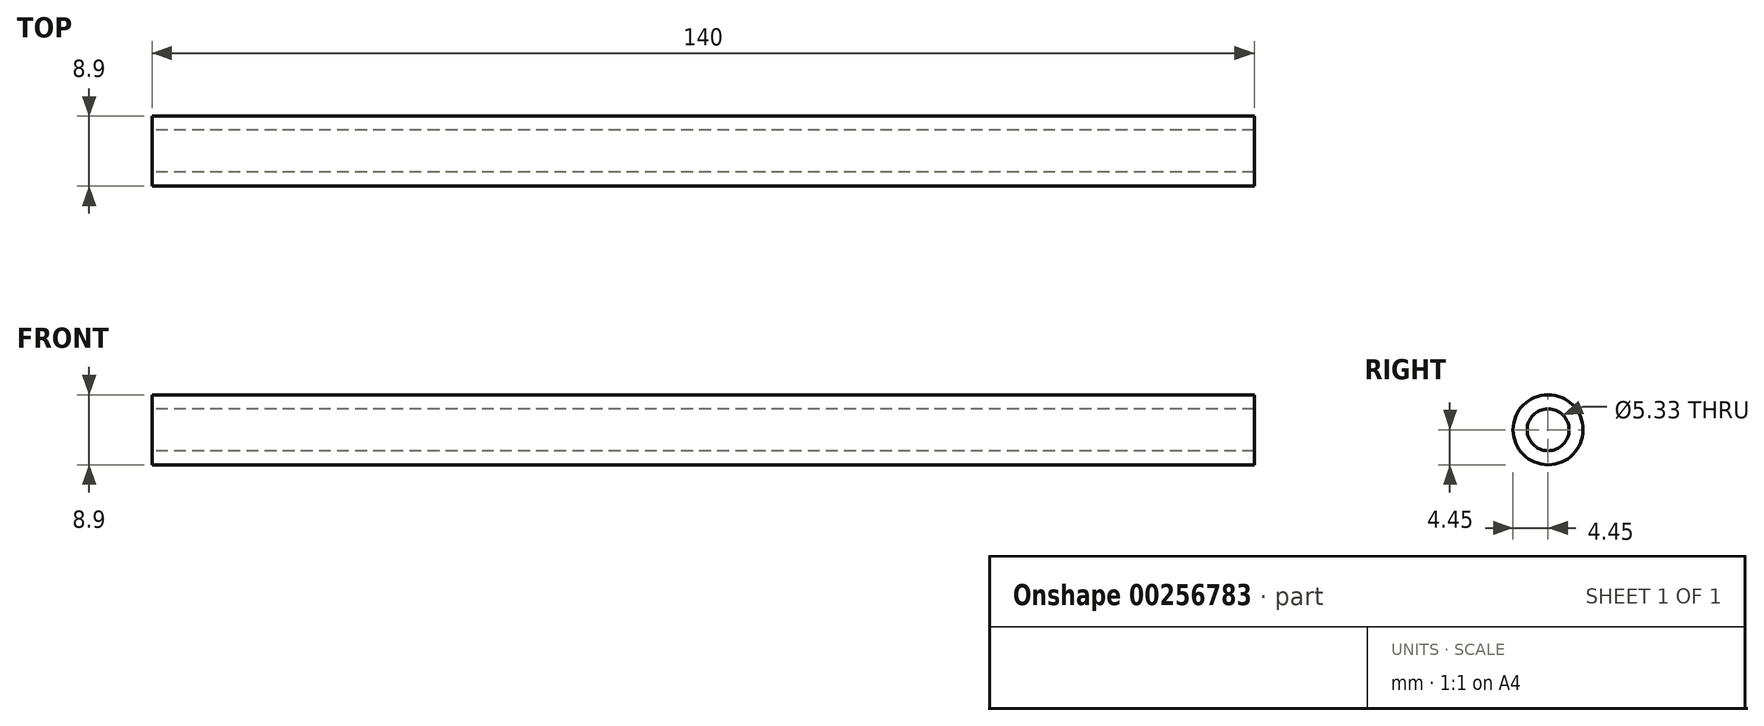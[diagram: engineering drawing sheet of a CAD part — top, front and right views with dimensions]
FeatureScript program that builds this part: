
annotation { "Feature Type Name" : "Feature", "Feature Type Description" : "" }
export const myFeature = defineFeature(function(context is Context, id is Id, definition is map)
    precondition{}
    {
        {
            var Q0;
            Q0=qCreatedBy(makeId("Right.planeOp"),FACE);
            var sketch = newSketch(context, id + "F0", { "sketchPlane" : qUnion([Q0])});
            skCircle(sketch, "E0", {"center": v(0, 0) * mm, "radius": 2.66 * mm});
            skCircle(sketch, "E1", {"center": v(0, 0) * mm, "radius": 4.45 * mm});
            skSolve(sketch);
        }
        {
            var Q0;
            Q0 = qSketchRegion(id + "F0", true);
            var Q1;
            Q1=makeQuery(id+"F0.imprint","IMPRINT",FACE,{"disambiguationData":[TD([[makeQuery(id+"F0.imprint","IMPRINT",EDGE,{"derivedFrom":sQuery(id+"F0.wireOp",EDGE,"E0")}),-1.0]])]});
            extrude(context, id + "F1", {"entities" : qUnion([Q0, Q1]), "depth" : 140 * mm});
        }
    });
